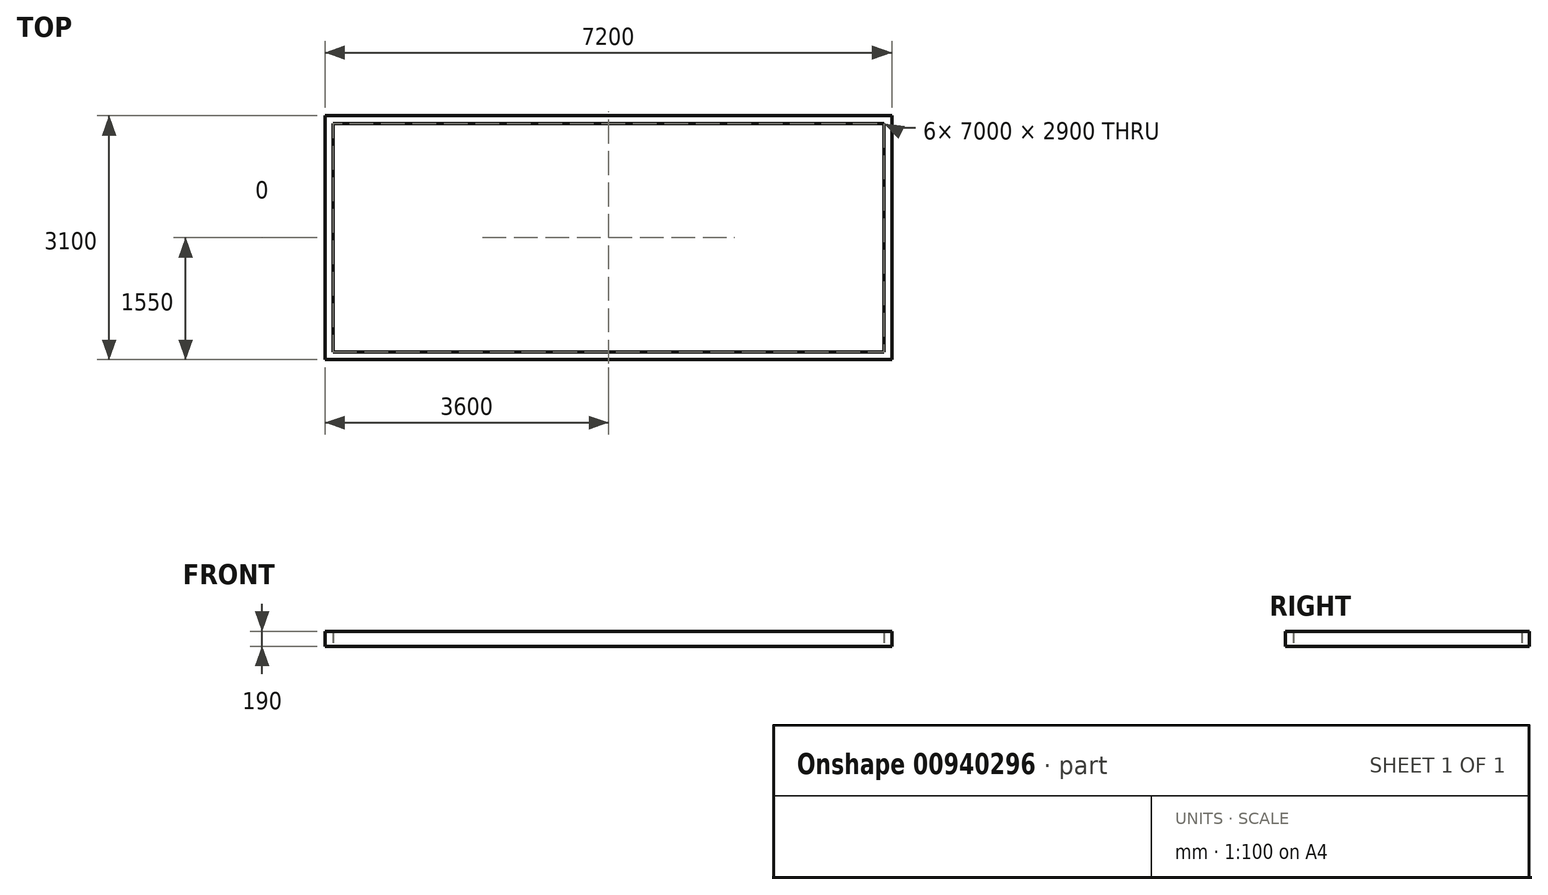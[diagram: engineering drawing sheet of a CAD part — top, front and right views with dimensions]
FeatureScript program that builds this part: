
annotation { "Feature Type Name" : "Feature", "Feature Type Description" : "" }
export const myFeature = defineFeature(function(context is Context, id is Id, definition is map)
    precondition{}
    {
        {
            var Q0;
            Q0=qCreatedBy(makeId("Top.planeOp"),FACE);
            var sketch = newSketch(context, id + "F0", { "sketchPlane" : qUnion([Q0])});
            skLineSegment(sketch, "E0.bottom", {"start": v(-3600.42, 1261.55) * mm, "end": v(3599.58, 1261.55) * mm});
            skLineSegment(sketch, "E0.top", {"start": v(-3600.42, -1838.45) * mm, "end": v(3599.58, -1838.45) * mm});
            skLineSegment(sketch, "E0.left", {"start": v(-3600.42, 1261.55) * mm, "end": v(-3600.42, -1838.45) * mm});
            skLineSegment(sketch, "E0.right", {"start": v(3599.58, 1261.55) * mm, "end": v(3599.58, -1838.45) * mm});
            skLineSegment(sketch, "E1.0", {"start": v(-3500.42, 1161.55) * mm, "end": v(3499.58, 1161.55) * mm});
            skLineSegment(sketch, "E1.1", {"start": v(-3500.42, 1161.55) * mm, "end": v(-3500.42, -1738.45) * mm});
            skLineSegment(sketch, "E1.2", {"start": v(-3500.42, -1738.45) * mm, "end": v(3499.58, -1738.45) * mm});
            skLineSegment(sketch, "E1.3", {"start": v(3499.58, 1161.55) * mm, "end": v(3499.58, -1738.45) * mm});
            skSolve(sketch);
        }
        {
            var Q0;
            Q0 = qSketchRegion(id + "F0", true);
            extrude(context, id + "F1", {"entities" : qUnion([Q0]), "depth" : 190 * mm, "offsetDistance" : 25 * mm});
        }
    });
